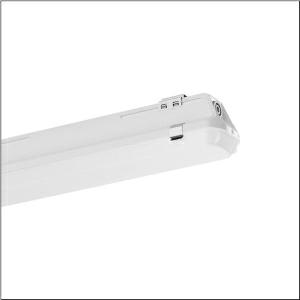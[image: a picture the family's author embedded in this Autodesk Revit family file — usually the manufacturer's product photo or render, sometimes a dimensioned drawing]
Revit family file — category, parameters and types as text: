
# Revit family: monsun_r__11_51fp109p460h_b614
name_source: partatom
category: Lighting Fixtures
units: mm (PartAtom-declared; Revit-internal decimal feet)

## family parameters
Cut with Voids When Loaded = No
Host = Face
Light Source = No
Part Type = Normal
Room Calculation Point = No
Round Connector Dimension = Use Diameter
Shared = No

## types (1)
- Monsun® 11 (1 x LED, 6100 lm, 34 W, 4000K)
    Apparent Load = 34 VA
    CIE Flux Codes = 47 77 93 94 100
    Color Rendering = 80
    Color Temperature = 4000K
    Default Elevation = 1800 mm
    Description = Monsun® 11, damp-proof luminaire, chain hanger, primary optical cover: enclosure, of PMMA, light emission: direct distribution, primary light characteristic: symmetric, installation type: suspended mounting, surface-mounted, horizontal mounting, vertical mounting, LED, rated luminous flux: 6.100lm, luminous efficacy: 179lm/W, light colour: 840, colour temperature: 4000K, control gear: ECG, with terminal, 3-pole, max. 2.5mm², mains connection: 220..240V, AC, 50/60Hz, start of lifetime: 34W, end of service life: 38W, luminaire housing, of glass-fibre reinforced polyester, uncoated, bright grey, incl. chain hanger, length: 1.590mm, width: 90mm, height: 88mm, clip for enclosure, of stainless steel (V2A), ceiling mounting element, of stainless steel (V2A), chain hanger, of stainless steel (V2A), protection rating (complete): IP66, insulation class (complete): insulation class I (protective earthing), certification: CE, ENEC, VDE, UKCA, protection symbol: D, impact resistance: IK04, permissible operating ambient temperature: -35..+40°C, standard: EN 50419, EN 60598-2-1, no direct snow, no direct sun, no direct rain, for indoor or canopied outdoor use, corresponds to IFS (International Featured Standards) requirements for safety and quality in the food industry, contact your sales advisor before using the luminaires in applications with unclear chemical exposure, large temperature fluctuations or condensation-forming humidity, LABS conformity tested according to VDMA 24364:2018-05, packaging unit: 1 piece
    Height = 89 mm
    Lamp = 1 x LED
    Lamp Light Flux = 6100 lm
    Lamp Power = 34 W
    Lamp count = 1
    Length = 1590 mm
    Luminous efficacy = 179 lm/W
    Manufacturer = Siteco
    ModVariant = No
    Model = 51FP109P460H
    Mounting Place = Ceiling
    Mounting Type = Surface mounted
    Number of Poles = 1
    OnlyDefault = Yes
    Power Factor = 1
    Product Name = Monsun® 11
    Product group = damp-proof luminaire
    ProductGroupID = 300
    Protection Class = Protection class I
    Protection Degree = IP 66
    RLX_Detail_Level = 1
    RLX_Emergency_Light_Flux = 0 lm
    RLX_Emergency_Type = 0
    RLX_Emergency_Type_DB = No
    RlxData = <blob elided: 88453 chars, md5=b5ece645>
    Socket = socket
    Standby Power = 0 W
    System Light Flux = 6100 lm
    System Power = 34 W
    Type Comments = Product without accessories
    Type Image = l_1004748.jpg
    URL = http://relux.com
    VarID = ---
    Voltage = 0 V
    Weight = 0.00 kg
    Width = 90 mm

## geometry (parser evidence)
native form markers: Blend x4, Sweep x13
no freeform markers — native parametric forms only
